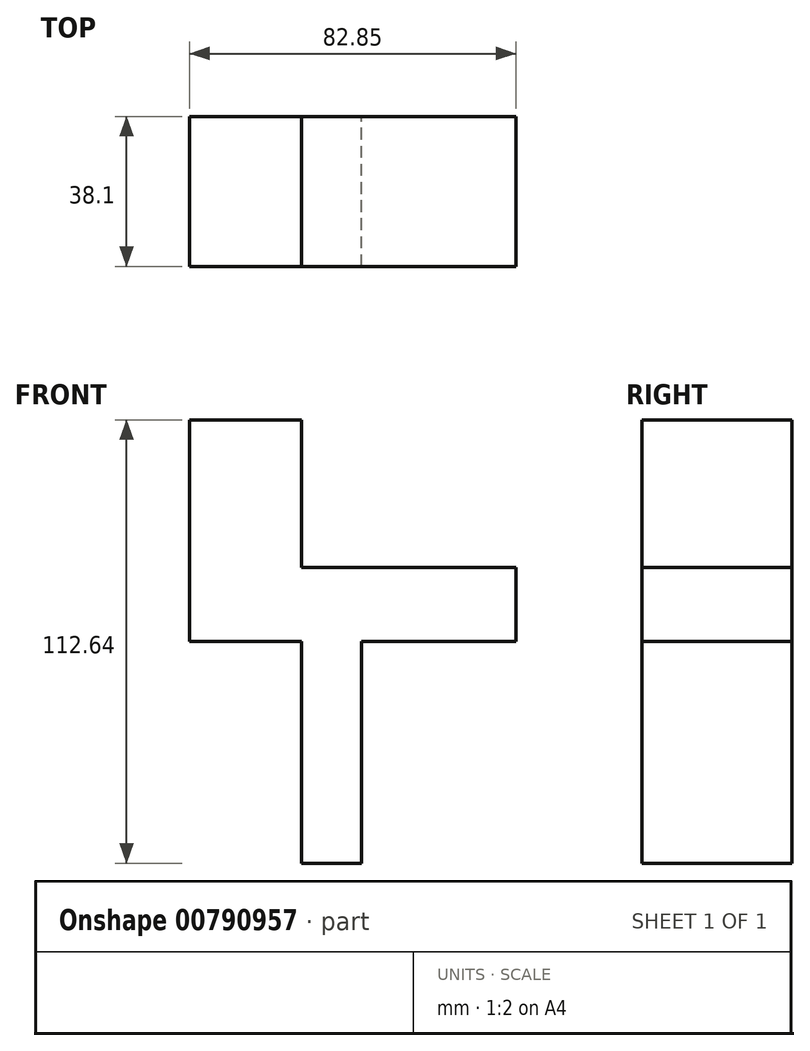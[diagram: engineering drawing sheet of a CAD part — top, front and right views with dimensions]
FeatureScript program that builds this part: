
annotation { "Feature Type Name" : "Feature", "Feature Type Description" : "" }
export const myFeature = defineFeature(function(context is Context, id is Id, definition is map)
    precondition{}
    {
        {
            var Q0;
            Q0=qCreatedBy(makeId("Front.planeOp"),FACE);
            var sketch = newSketch(context, id + "F0", { "sketchPlane" : qUnion([Q0])});
            skLineSegment(sketch, "E0", {"start": v(-47.52, 0) * mm, "end": v(-47.52, -56.32) * mm});
            skLineSegment(sketch, "E1", {"start": v(-47.52, -56.32) * mm, "end": v(-32.2, -56.32) * mm});
            skLineSegment(sketch, "E2", {"start": v(-32.2, -56.32) * mm, "end": v(-32.2, 0) * mm});
            skLineSegment(sketch, "E3", {"start": v(-47.52, 0) * mm, "end": v(-75.9, 0) * mm});
            skLineSegment(sketch, "E4", {"start": v(-75.9, 0) * mm, "end": v(-75.9, 56.32) * mm});
            skLineSegment(sketch, "E5", {"start": v(-75.9, 56.32) * mm, "end": v(-47.52, 56.32) * mm});
            skLineSegment(sketch, "E6", {"start": v(-47.52, 56.32) * mm, "end": v(-47.52, 18.87) * mm});
            skLineSegment(sketch, "E7", {"start": v(-47.52, 18.87) * mm, "end": v(6.95, 18.87) * mm});
            skLineSegment(sketch, "E8", {"start": v(6.95, 18.87) * mm, "end": v(6.95, 0) * mm});
            skLineSegment(sketch, "E9", {"start": v(6.95, 0) * mm, "end": v(-32.2, 0) * mm});
            skSolve(sketch);
        }
        {
            var Q0;
            Q0=makeQuery(id+"F0.imprint","IMPRINT",FACE,{"disambiguationData":[TD([[makeQuery(id+"F0.imprint","IMPRINT",EDGE,{"derivedFrom":sQuery(id+"F0.wireOp",EDGE,"E0")}),1.0]])]});
            extrude(context, id + "F1", {"entities" : qUnion([Q0]), "depth" : 38.1 * mm, "offsetDistance" : 25.4 * mm});
        }
    });
